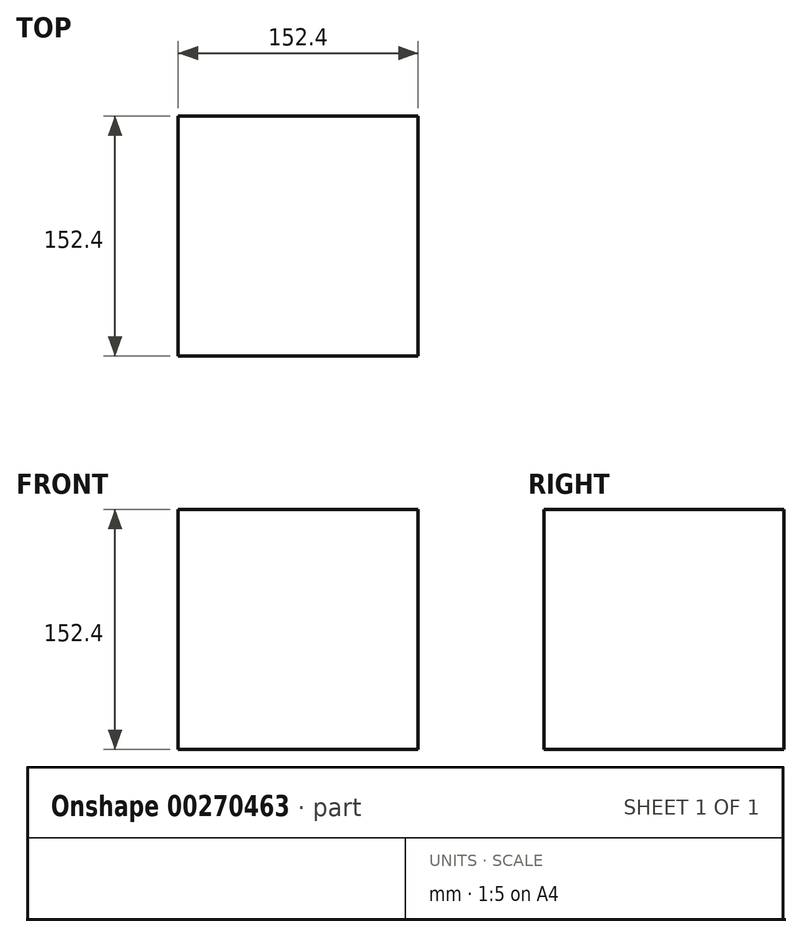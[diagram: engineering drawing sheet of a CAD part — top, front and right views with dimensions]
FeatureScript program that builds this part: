
annotation { "Feature Type Name" : "Feature", "Feature Type Description" : "" }
export const myFeature = defineFeature(function(context is Context, id is Id, definition is map)
    precondition{}
    {
        {
            var Q0;
            Q0=qCreatedBy(makeId("Top.planeOp"),FACE);
            var sketch = newSketch(context, id + "F0", { "sketchPlane" : qUnion([Q0])});
            skLineSegment(sketch, "E0", {"start": v(0, 0) * mm, "end": v(0, -152.4) * mm});
            skLineSegment(sketch, "E1", {"start": v(0, -152.4) * mm, "end": v(152.4, -152.4) * mm});
            skLineSegment(sketch, "E2", {"start": v(152.4, -152.4) * mm, "end": v(152.4, 0) * mm});
            skLineSegment(sketch, "E3", {"start": v(152.4, 0) * mm, "end": v(0, 0) * mm});
            skSolve(sketch);
        }
        {
            var Q0;
            Q0 = qSketchRegion(id + "F0", true);
            extrude(context, id + "F1", {"entities" : qUnion([Q0]), "depth" : 152.4 * mm});
        }
    });
